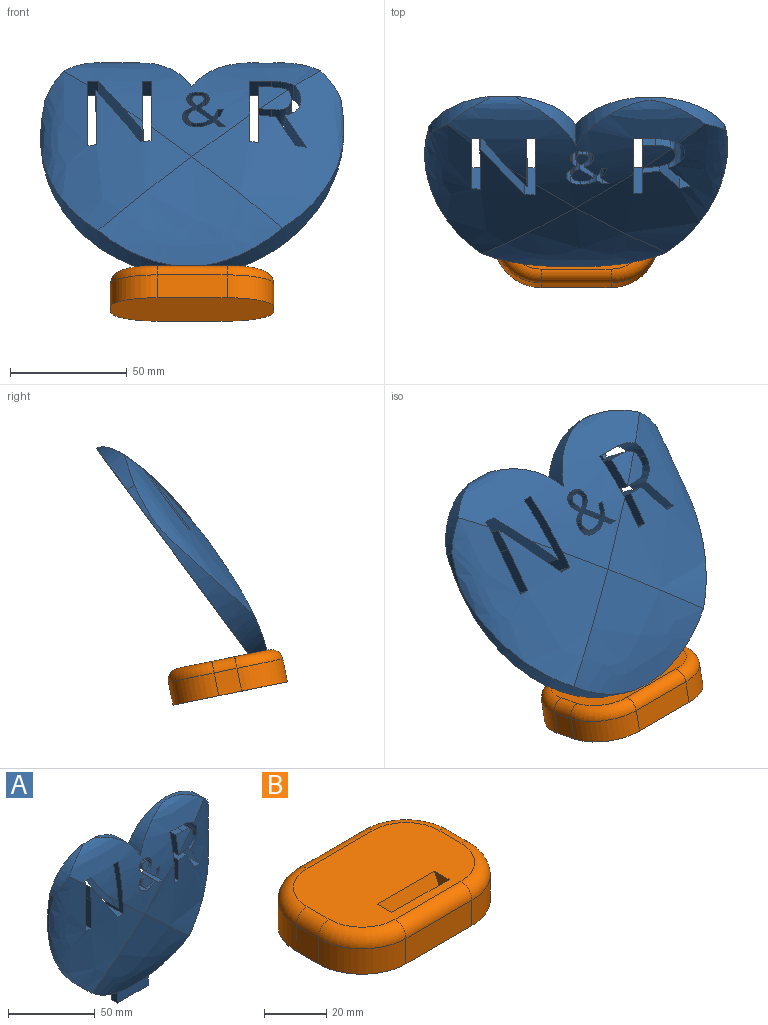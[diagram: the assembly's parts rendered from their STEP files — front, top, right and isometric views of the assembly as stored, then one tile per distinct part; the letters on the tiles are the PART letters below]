
ASSEMBLY  parts=2 mates=1
PART A: 103 faces, bbox 137x15.4x121.8 mm
  f0: extruded ~12.34x1.96mm, area 23.3mm2, adj f1,f6,f7,f9,f91,f92
  f1: extruded ~6.23x5.27mm, area 22.3mm2, adj f0,f2,f3,f4,f5,f6,f7,f8
  f2: extruded ~13.19x2.04mm, area 34.5mm2, adj f1,f3,f8,f9
  f3: extruded ~13.19x2.43mm, area 40.4mm2, adj f1,f2,f4,f9
  f4: extruded ~12.93x1.99mm, area 27.4mm2, adj f1,f3,f5,f9
  f5: extruded ~12.62x1.7mm, area 23.6mm2, adj f1,f4,f6,f9
  f6: extruded ~12.34x1.86mm, area 23.5mm2, adj f0,f1,f5,f9,f90,f92
  f7: extruded ~12.63x1.75mm, area 24.6mm2, adj f0,f1,f8,f9
  f8: extruded ~12.91x1.78mm, area 23.9mm2, adj f1,f2,f7,f9
  f9: plane 136.53x121.34mm, normal (0,1,0), area 11038.8mm2, adj f0,f2,f3,f4,f5,f6,f7,f8
  f10: extruded ~14.29x2.8mm, area 41.6mm2, adj f9,f11,f12,f13,f94,f95
  f11: extruded ~9.28x7.84mm, area 42mm2, adj f10,f12,f13,f14,f15,f16,f17
  f12: extruded ~14.29x5.43mm, area 82.1mm2, adj f9,f10,f11,f17,f93,f95
  f13: extruded ~14.21x2.52mm, area 39.7mm2, adj f9,f10,f11,f14
  f14: extruded ~13.99x1.57mm, area 22.4mm2, adj f9,f11,f13,f15
  f15: extruded ~13.83x1.3mm, area 22mm2, adj f9,f11,f14,f16
  f16: extruded ~13.69x2.13mm, area 35.7mm2, adj f9,f11,f15,f17
  f17: plane 14.17x5.99mm, normal (0.7,0,0.72), area 114.2mm2, adj f9,f11,f12,f16
  f18: extruded ~13.27x12.28mm, area 91.8mm2, adj f19,f22,f23,f24,f25,f26
  f19: extruded ~13.75x11.3mm, area 68.3mm2, adj f18,f20,f21,f22,f26
  f20: extruded ~11.71x5.09mm, area 65.1mm2, adj f9,f19,f21,f26
  f21: extruded ~12.74x6.26mm, area 81.2mm2, adj f9,f19,f20,f22
  f22: plane 13.44x5.54mm, normal (0,0,-1), area 68.6mm2, adj f9,f18,f19,f21,f23,f27,f28,f29
  f23: plane 13.44x13.27mm, normal (-1,0,0), area 164.9mm2, adj f9,f18,f22,f24
  f24: plane 11.2x5.25mm, normal (0,0,1), area 54.8mm2, adj f9,f18,f23,f25,f96,f97,f98
  f25: extruded ~11.53x6.52mm, area 77.2mm2, adj f9,f18,f24,f26
  f26: extruded ~11.62x4.96mm, area 63.9mm2, adj f9,f18,f19,f20,f25
  f27: plane 3.46x2mm, normal (-1,0,0), area 6.9mm2, adj f9,f22,f29,f73
  f28: plane 3.46x2mm, normal (1,0,0), area 6.9mm2, adj f9,f22,f29,f73
  f29: plane 3.46x2mm, normal (0,-1,0), area 6.9mm2, adj f22,f27,f28,f73
  f30: extruded ~14.44x4.52mm, area 68.6mm2, adj f9,f35,f61,f62,f94,f95
  f31: extruded ~12.1x3.7mm, area 44.6mm2, adj f9,f35,f47,f48,f91,f92
  f32: extruded ~12.51x8.35mm, area 20.9mm2, adj f35,f76,f77,f84,f85
  f33: extruded ~87.78x64.77mm, area 2906.5mm2, adj f35,f36,f37,f38,f39,f75,f78,f79
  f34: extruded ~86.93x65mm, area 2839.9mm2, adj f9,f35,f37,f38,f40,f42,f64,f67
  f35: extruded ~110.1x60mm, area 2912.5mm2, adj f9,f30,f31,f32,f33,f34,f39,f40
  f36: extruded ~0.11x0.1mm, area 0mm2, adj f33,f88,f89
  f37: extruded ~79.17x52.88mm, area 2363.7mm2, adj f33,f34,f38
  f38: extruded ~129.77x90.89mm, area 1547.3mm2, adj f9,f33,f34,f37,f39,f99,f100,f101
  f39: cylinder r=33.81mm len=26.2mm, axis (0,1,0), area 187mm2, adj f9,f33,f35,f38
  f40: cylinder r=35.84mm len=63.88mm, axis (0,1,0), area 441mm2, adj f9,f34,f35,f41,f42
  f41: cylinder r=33.81mm len=25.44mm, axis (0,1,0), area 224.3mm2, adj f9,f35,f40
  f42: extruded ~9.24x2.78mm, area 13mm2, adj f9,f34,f40
  f43: extruded ~13.67x3.38mm, area 59.1mm2, adj f9,f35,f44,f63
  f44: extruded ~13.33x1.96mm, area 33.2mm2, adj f9,f35,f43,f45
  f45: extruded ~13.07x1.38mm, area 19.9mm2, adj f9,f35,f44,f46
  f46: extruded ~12.87x1.49mm, area 19.4mm2, adj f9,f35,f45,f47
  f47: extruded ~12.64x3.18mm, area 44mm2, adj f9,f31,f35,f46
  f48: extruded ~12.09x3.46mm, area 43.4mm2, adj f9,f31,f35,f49,f90,f92
  f49: extruded ~12.63x3.16mm, area 43.4mm2, adj f9,f35,f48,f50
  f50: extruded ~13.04x2.68mm, area 37mm2, adj f9,f35,f49,f51
  f51: extruded ~13.37x3.05mm, area 52.3mm2, adj f9,f35,f50,f52
  f52: plane 14.02x5.57mm, normal (-0.69,0,-0.72), area 104.7mm2, adj f9,f35,f51,f53
  f53: extruded ~13.97x1.97mm, area 32.3mm2, adj f9,f35,f52,f54
  f54: extruded ~13.77x2.48mm, area 35.4mm2, adj f9,f35,f53,f55
  f55: plane 13.48x2.28mm, normal (0,0,-1), area 30.7mm2, adj f9,f35,f54,f56
  f56: extruded ~14.1x5.89mm, area 90.7mm2, adj f9,f35,f55,f57
  f57: plane 14.44x4.08mm, normal (-0.7,0,-0.72), area 80.7mm2, adj f9,f35,f56,f58
  f58: plane 14.42x3.1mm, normal (0,0,1), area 44.8mm2, adj f9,f35,f57,f59
  f59: plane 14.43x2.52mm, normal (0.69,0,0.72), area 49.9mm2, adj f9,f35,f58,f60
  f60: extruded ~14.4x3.26mm, area 55.5mm2, adj f9,f35,f59,f61
  f61: extruded ~14.44x3.69mm, area 51.5mm2, adj f9,f30,f35,f60,f93,f95
  f62: extruded ~14.34x3.97mm, area 62.6mm2, adj f9,f30,f35,f63
  f63: extruded ~13.99x3.12mm, area 45.8mm2, adj f9,f35,f43,f62
  f64: plane 34.7x13.87mm, normal (1,0,0), area 450.5mm2, adj f9,f34,f35,f65,f68
  f65: plane 10.35x9.52mm, normal (0,0,-1), area 94.5mm2, adj f9,f35,f64,f66,f96,f97,f98
  f66: extruded ~10.95x9.44mm, area 105.5mm2, adj f9,f35,f65,f67
  f67: extruded ~11.02x7.36mm, area 87.8mm2, adj f9,f34,f35,f66,f69
  f68: plane 13.87x4.03mm, normal (0,0,1), area 55.1mm2, adj f9,f34,f64,f74
  f69: extruded ~11.86x9.3mm, area 139.9mm2, adj f9,f34,f67,f70
  f70: plane 16.04x12.31mm, normal (-0.86,0,-0.52), area 198.6mm2, adj f9,f34,f69,f71
  f71: plane 10.95x4.77mm, normal (0,0,1), area 49.6mm2, adj f9,f34,f70,f72
  f72: plane 14.71x12.76mm, normal (0.86,0,0.5), area 196.3mm2, adj f9,f34,f71,f73
  f73: plane 13.45x7.25mm, normal (0,0,1), area 90.1mm2, adj f9,f27,f28,f29,f34,f72,f74
  f74: plane 14.43x13.45mm, normal (-1,0,0), area 194.1mm2, adj f9,f34,f68,f73
  f75: plane 14.45x4.6mm, normal (0,0,1), area 65.8mm2, adj f9,f33,f81,f89
  f76: extruded ~14.21x4.12mm, area 58.5mm2, adj f9,f32,f77,f84
  f77: plane 14.21x0.19mm, normal (0,0,-1), area 2.7mm2, adj f9,f32,f76,f85
  f78: plane 11.68x3.73mm, normal (0,0,1), area 42.2mm2, adj f9,f33,f79,f87
  f79: plane 19.73x11.68mm, normal (-1,0,0), area 230.4mm2, adj f9,f33,f78,f80
  f80: extruded ~11.68x9.4mm, area 109.5mm2, adj f9,f33,f79,f88
  f81: plane 34.7x14.45mm, normal (-1,0,0), area 456.9mm2, adj f9,f33,f35,f75,f82
  f82: plane 10.35x3.78mm, normal (0,0,-1), area 39.1mm2, adj f9,f35,f81,f83
  f83: plane 19.92x13.8mm, normal (1,0,0), area 245.5mm2, adj f9,f35,f82,f84
  f84: extruded ~14.19x4.98mm, area 69.9mm2, adj f9,f32,f35,f76,f83
  f85: plane 29.12x19.04mm, normal (-0.84,0,-0.55), area 444mm2, adj f9,f32,f35,f77,f86
  f86: plane 10.35x4.56mm, normal (0,0,-1), area 47.2mm2, adj f9,f35,f85,f87
  f87: plane 34.7x10.93mm, normal (1,0,0), area 378.7mm2, adj f9,f33,f35,f78,f86
  f88: plane 11.64x0.19mm, normal (0,0,1), area 2.2mm2, adj f9,f33,f36,f80,f89
  f89: plane 29.12x18.97mm, normal (0.84,0,0.55), area 453.3mm2, adj f9,f33,f36,f75,f88
  f90: plane 2x1.9mm, normal (1,0,0), area 3.8mm2, adj f6,f9,f48,f92
  f91: plane 2x1.99mm, normal (-1,0,0), area 4mm2, adj f0,f9,f31,f92
  f92: plane 2.13x2.04mm, normal (0,-1,0), area 3.8mm2, adj f0,f6,f31,f48,f90,f91
  f93: plane 2.04x2mm, normal (1,0,0), area 4.1mm2, adj f9,f12,f61,f95
  f94: plane 2.04x2mm, normal (-1,0,0), area 4.1mm2, adj f9,f10,f30,f95
  f95: plane 2.12x2.01mm, normal (0,-1,0), area 4.1mm2, adj f10,f12,f30,f61,f93,f94
  f96: plane 3.54x2mm, normal (-1,0,0), area 7.1mm2, adj f9,f24,f65,f98
  f97: plane 3.54x2mm, normal (1,0,0), area 7.1mm2, adj f9,f24,f65,f98
  f98: plane 3.54x2mm, normal (0,-1,0), area 7.1mm2, adj f24,f65,f96,f97
  f99: plane 25.13x10.43mm, normal (0,-1,0), area 225mm2, adj f38,f100,f101,f102
  f100: plane 10.36x5mm, normal (1,0,0), area 51.8mm2, adj f9,f38,f99,f102
  f101: plane 9.7x5mm, normal (-1,0,0), area 48.5mm2, adj f9,f38,f99,f102
  f102: plane 25x5mm, normal (0,0,-1), area 125mm2, adj f9,f99,f100,f101
PART B: 23 faces, bbox 73.3x53.3x15 mm
  f0: plane 60x40mm, normal (0,0,1), area 2034.7mm2, adj f6,f7,f9,f10,f11,f12,f13,f14
  f1: plane 10x10mm, normal (-1,0,0), area 100mm2, adj f2,f14,f15,f17
  f2: plane 70x50mm, normal (0,0,-1), area 3156.6mm2, adj f1,f3,f4,f5,f15,f17,f19,f21
  f3: plane 10x10mm, normal (1,0,0), area 100mm2, adj f2,f11,f19,f21
  f4: plane 30x10mm, normal (0,-1,0), area 300mm2, adj f2,f12,f17,f21
  f5: plane 30x10mm, normal (0,1,0), area 300mm2, adj f2,f13,f15,f19
  f6: plane 26x11.71mm, normal (0,-0.91,0.42), area 335.9mm2, adj f0,f8,f9,f10
  f7: plane 26x9.17mm, normal (0,0.91,-0.42), area 263.1mm2, adj f0,f8,f9,f10
  f8: plane 26x5.44mm, normal (0,0.42,0.91), area 156mm2, adj f6,f7,f9,f10
  f9: plane 11.71x10.9mm, normal (1,0,0), area 69.1mm2, adj f0,f6,f7,f8
  f10: plane 11.71x10.9mm, normal (-1,0,0), area 69.1mm2, adj f0,f6,f7,f8
  f11: cylinder r=5mm len=10mm, axis (0,1,0), area 78.5mm2, adj f0,f3,f20,f22
  f12: cylinder r=5mm len=30mm, axis (1,0,0), area 235.6mm2, adj f0,f4,f18,f22
  f13: cylinder r=5mm len=30mm, axis (-1,0,0), area 235.6mm2, adj f0,f5,f16,f20
  f14: cylinder r=5mm len=10mm, axis (0,-1,0), area 78.5mm2, adj f0,f1,f16,f18
  f15: cylinder r=20mm len=20mm, axis (0,0,-1), area 314.2mm2, adj f1,f2,f5,f16
  f16: torus R=15mm, axis (0,0,1), area 224.3mm2, adj f0,f13,f14,f15
  f17: cylinder r=20mm len=20mm, axis (0,0,1), area 314.2mm2, adj f1,f2,f4,f18
  f18: torus R=15mm, axis (0,0,1), area 224.3mm2, adj f0,f12,f14,f17
  f19: cylinder r=20mm len=20mm, axis (0,0,1), area 314.2mm2, adj f2,f3,f5,f20
  f20: torus R=15mm, axis (0,0,1), area 224.3mm2, adj f0,f11,f13,f19
  f21: cylinder r=20mm len=20mm, axis (0,0,-1), area 314.2mm2, adj f2,f3,f4,f22
  f22: torus R=15mm, axis (0,0,1), area 224.3mm2, adj f0,f11,f12,f21
PLACE A rot(axis=(-1,0,0),36.5deg) t=(-0.3,22.16,-24.47)mm
PLACE B rot(axis=(-1,0,0),11.5deg) t=(-0.15,17.06,-0.43)mm
MATE fastened A.f99 <-> B.f7  axis (0,-0.8,0.6) through (-0.15,-15.68,-67.15)mm
